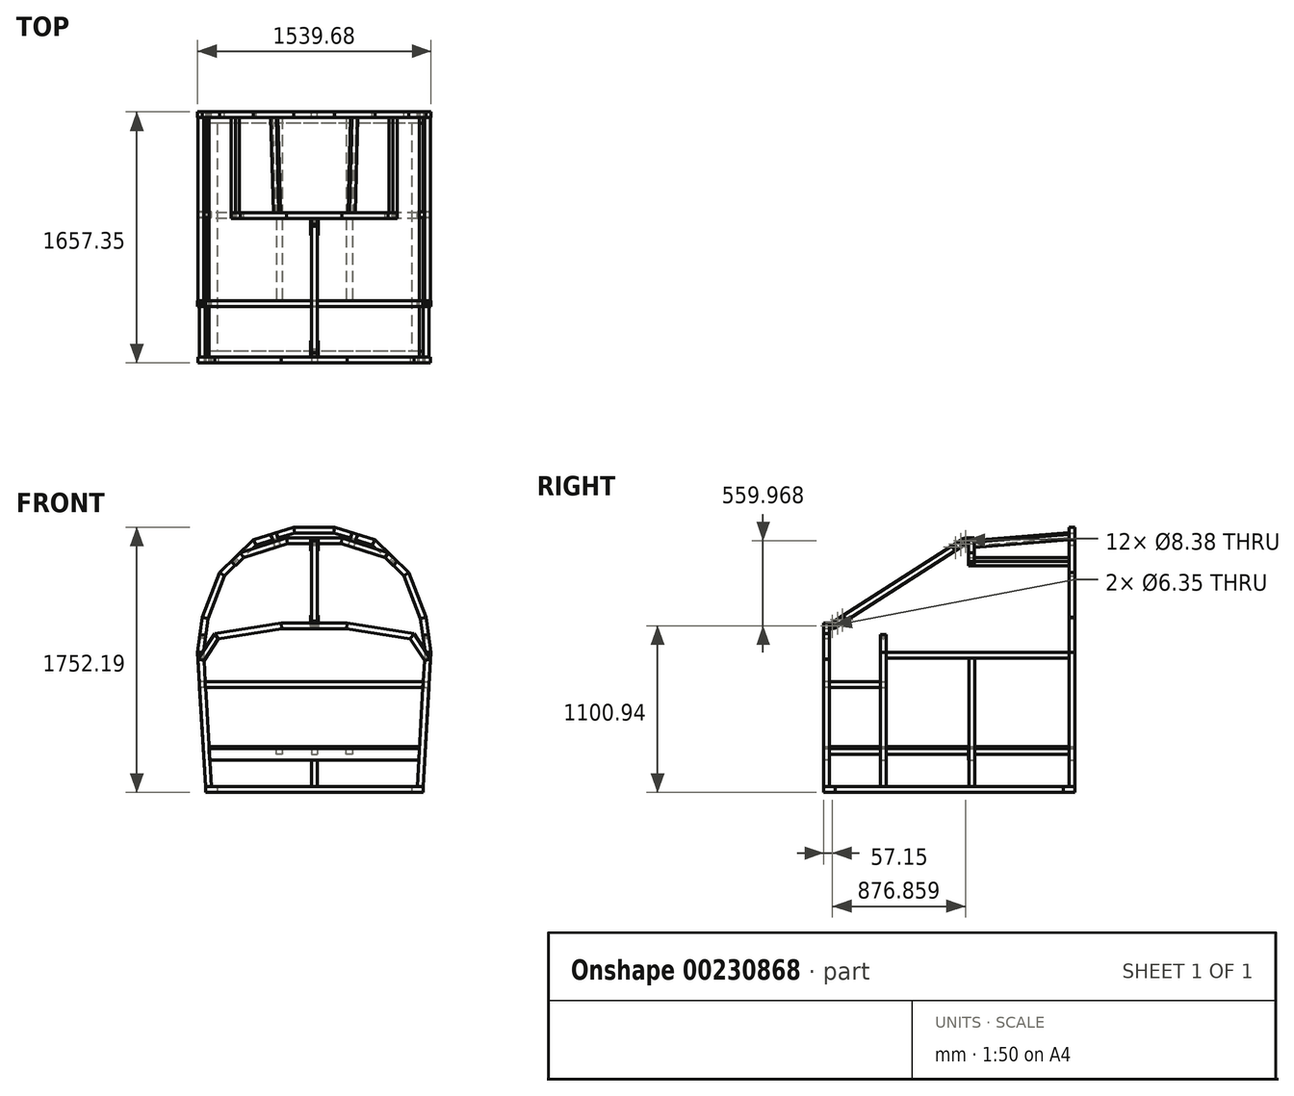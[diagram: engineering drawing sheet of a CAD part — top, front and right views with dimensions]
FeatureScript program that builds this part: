
annotation { "Feature Type Name" : "Feature", "Feature Type Description" : "" }
export const myFeature = defineFeature(function(context is Context, id is Id, definition is map)
    precondition{}
    {
        {
            var Q0;
            Q0=qCreatedBy(makeId("Front.planeOp"),FACE);
            var sketch = newSketch(context, id + "F0", { "sketchPlane" : qUnion([Q0])});
            skLineSegment(sketch, "E0", {"start": v(0, 0) * mm, "end": v(717.55, 0) * mm});
            skLineSegment(sketch, "E1", {"start": v(717.55, 0) * mm, "end": v(717.55, 38.1) * mm});
            skLineSegment(sketch, "E2", {"start": v(717.55, 38.1) * mm, "end": v(0, 38.1) * mm});
            skLineSegment(sketch, "E3.MirrorCS", {"start": v(-717.55, 38.1) * mm, "end": v(0, 38.1) * mm});
            skLineSegment(sketch, "E4.MirrorCS", {"start": v(0, 0) * mm, "end": v(-717.55, 0) * mm});
            skLineSegment(sketch, "E5.MirrorCS", {"start": v(-717.55, 0) * mm, "end": v(-717.55, 38.1) * mm});
            skSolve(sketch);
        }
        {
            var Q0;
            Q0 = qSketchRegion(id + "F0", true);
            extrude(context, id + "F1", {"entities" : qUnion([Q0]), "oppositeDirection" : true, "depth" : 76.2 * mm});
        }
        {
            var Q0;
            Q0=makeQuery(id+"F1.opExtrude","CAP_FACE",FACE,{"disambiguationData":[OSD([sQuery(id+"F0.wireOp",EDGE,"E0"),sQuery(id+"F0.wireOp",EDGE,"E1"),sQuery(id+"F0.wireOp",EDGE,"E2"),sQuery(id+"F0.wireOp",EDGE,"E3.MirrorCS"),sQuery(id+"F0.wireOp",EDGE,"E4.MirrorCS"),sQuery(id+"F0.wireOp",EDGE,"E5.MirrorCS")])],"isStart":false});
            var sketch = newSketch(context, id + "F2", { "sketchPlane" : qUnion([Q0])});
            skLineSegment(sketch, "E6.bottom", {"start": v(-717.55, 38.1) * mm, "end": v(-641.35, 38.1) * mm});
            skLineSegment(sketch, "E6.top", {"start": v(-717.55, 0) * mm, "end": v(-641.35, 0) * mm});
            skLineSegment(sketch, "E6.left", {"start": v(-717.55, 38.1) * mm, "end": v(-717.55, 0) * mm});
            skLineSegment(sketch, "E6.right", {"start": v(-641.35, 38.1) * mm, "end": v(-641.35, 0) * mm});
            skLineSegment(sketch, "E7.MirrorCS", {"start": v(641.35, 38.1) * mm, "end": v(641.35, 0) * mm});
            skLineSegment(sketch, "E8.MirrorCS", {"start": v(717.55, 38.1) * mm, "end": v(717.55, 0) * mm});
            skLineSegment(sketch, "E9.MirrorCS", {"start": v(717.55, 0) * mm, "end": v(641.35, 0) * mm});
            skLineSegment(sketch, "E10.MirrorCS", {"start": v(717.55, 38.1) * mm, "end": v(641.35, 38.1) * mm});
            skSolve(sketch);
        }
        {
            var Q0;
            Q0 = qSketchRegion(id + "F2", true);
            extrude(context, id + "F3", {"entities" : qUnion([Q0]), "depth" : 1504.95 * mm});
        }
        {
            var Q0;
            Q0=makeQuery(id+"F3.opExtrude","CAP_FACE",FACE,{"disambiguationData":[OSD([sQuery(id+"F2.wireOp",EDGE,"E6.bottom"),sQuery(id+"F2.wireOp",EDGE,"E6.top"),sQuery(id+"F2.wireOp",EDGE,"E6.left"),sQuery(id+"F2.wireOp",EDGE,"E6.right")])],"isStart":false});
            var sketch = newSketch(context, id + "F4", { "sketchPlane" : qUnion([Q0])});
            skPoint(sketch, "E11.0", {"position": v(717.55, 0) * mm});
            skLineSegment(sketch, "E12.bottom", {"start": v(-717.55, 38.1) * mm, "end": v(717.55, 38.1) * mm});
            skLineSegment(sketch, "E12.top", {"start": v(-717.55, 0) * mm, "end": v(717.55, 0) * mm});
            skLineSegment(sketch, "E12.left", {"start": v(-717.55, 38.1) * mm, "end": v(-717.55, 0) * mm});
            skLineSegment(sketch, "E12.right", {"start": v(717.55, 38.1) * mm, "end": v(717.55, 0) * mm});
            skSolve(sketch);
        }
        {
            var Q0;
            Q0 = qSketchRegion(id + "F4", true);
            extrude(context, id + "F5", {"entities" : qUnion([Q0]), "depth" : 76.2 * mm});
        }
        {
            var Q0;
            Q0=makeQuery(id+"F5.opExtrude","CAP_FACE",FACE,{"disambiguationData":[OSD([sQuery(id+"F4.wireOp",EDGE,"E12.bottom"),sQuery(id+"F4.wireOp",EDGE,"E12.top"),sQuery(id+"F4.wireOp",EDGE,"E12.left"),sQuery(id+"F4.wireOp",EDGE,"E12.right")])],"isStart":false});
            var sketch = newSketch(context, id + "F6", { "sketchPlane" : qUnion([Q0])});
            skLineSegment(sketch, "E13", {"start": v(-717.55, 290.98) * mm, "end": v(717.55, 290.98) * mm, "construction": true});
            skPoint(sketch, "E13.startSnap0", {"position": v(-717.55, 19.05) * mm});
            skPoint(sketch, "E14", {"position": v(-769.84, 926.08) * mm});
            skLineSegment(sketch, "E15", {"start": v(-769.84, 926.08) * mm, "end": v(-717.55, 38.1) * mm});
            skLineSegment(sketch, "E16", {"start": v(-717.55, 38.1) * mm, "end": v(-772.22, 38.1) * mm, "construction": true});
            skLineSegment(sketch, "E17.0", {"start": v(-731.59, 924.59) * mm, "end": v(-679.38, 38.1) * mm});
            skLineSegment(sketch, "E18", {"start": v(-717.55, 38.1) * mm, "end": v(-679.38, 38.1) * mm});
            skPoint(sketch, "E19", {"position": v(-737.87, 1158.11) * mm});
            skLineSegment(sketch, "E20", {"start": v(-769.84, 926.08) * mm, "end": v(-737.87, 1158.11) * mm});
            skLineSegment(sketch, "E21", {"start": v(-769.84, 926.08) * mm, "end": v(-776.64, 1041.51) * mm, "construction": true});
            skPoint(sketch, "E22", {"position": v(-623.49, 1451.13) * mm});
            skLineSegment(sketch, "E23", {"start": v(-737.87, 1158.11) * mm, "end": v(-623.49, 1451.13) * mm});
            skLineSegment(sketch, "E24", {"start": v(-737.87, 1158.11) * mm, "end": v(-724.69, 1253.8) * mm, "construction": true});
            skPoint(sketch, "E25", {"position": v(-133.82, 1752.2) * mm});
            skPoint(sketch, "E26", {"position": v(-402.75, 1667.92) * mm});
            skLineSegment(sketch, "E27", {"start": v(-623.49, 1451.13) * mm, "end": v(-402.75, 1667.92) * mm});
            skLineSegment(sketch, "E28", {"start": v(-623.49, 1451.13) * mm, "end": v(-586.53, 1545.8) * mm, "construction": true});
            skLineSegment(sketch, "E29", {"start": v(-402.75, 1667.92) * mm, "end": v(-133.82, 1752.2) * mm});
            skLineSegment(sketch, "E30", {"start": v(-402.75, 1667.92) * mm, "end": v(-358.73, 1711.15) * mm, "construction": true});
            skLineSegment(sketch, "E31", {"start": v(-133.82, 1752.2) * mm, "end": v(0, 1752.2) * mm});
            skLineSegment(sketch, "E32", {"start": v(-133.82, 1752.2) * mm, "end": v(-83.59, 1767.94) * mm, "construction": true});
            skLineSegment(sketch, "E33.0", {"start": v(-128, 1714.1) * mm, "end": v(0, 1714.1) * mm});
            skLineSegment(sketch, "E33.1", {"start": v(-731.59, 924.59) * mm, "end": v(-700.74, 1148.45) * mm});
            skLineSegment(sketch, "E33.2", {"start": v(-700.74, 1148.45) * mm, "end": v(-590.96, 1429.67) * mm});
            skLineSegment(sketch, "E33.3", {"start": v(-590.96, 1429.67) * mm, "end": v(-382.6, 1634.3) * mm});
            skLineSegment(sketch, "E33.4", {"start": v(-382.6, 1634.3) * mm, "end": v(-128, 1714.1) * mm});
            skLineSegment(sketch, "E34", {"start": v(-737.87, 1158.11) * mm, "end": v(-700.74, 1148.45) * mm});
            skLineSegment(sketch, "E35", {"start": v(-623.49, 1451.13) * mm, "end": v(-590.96, 1429.67) * mm});
            skLineSegment(sketch, "E36", {"start": v(-402.75, 1667.92) * mm, "end": v(-382.6, 1634.3) * mm});
            skLineSegment(sketch, "E37", {"start": v(-133.82, 1752.2) * mm, "end": v(-128, 1714.1) * mm});
            skLineSegment(sketch, "E38.MirrorCS", {"start": v(133.82, 1752.2) * mm, "end": v(0, 1752.2) * mm});
            skLineSegment(sketch, "E39.MirrorCS", {"start": v(128, 1714.1) * mm, "end": v(0, 1714.1) * mm});
            skLineSegment(sketch, "E40.MirrorCS", {"start": v(133.82, 1752.2) * mm, "end": v(128, 1714.1) * mm});
            skPoint(sketch, "E41.orphan", {"position": v(-731.67, 926.08) * mm});
            skLineSegment(sketch, "E42", {"start": v(-769.84, 926.08) * mm, "end": v(-731.59, 924.59) * mm});
            skLineSegment(sketch, "E43", {"start": v(0, 290.98) * mm, "end": v(-694.28, 290.98) * mm});
            skLineSegment(sketch, "E44", {"start": v(-689.79, 214.78) * mm, "end": v(0, 214.78) * mm});
            skLineSegment(sketch, "E45", {"start": v(-694.28, 290.98) * mm, "end": v(-689.79, 214.78) * mm});
            skLineSegment(sketch, "E46.MirrorCS", {"start": v(689.79, 214.78) * mm, "end": v(0, 214.78) * mm});
            skLineSegment(sketch, "E47.MirrorCS", {"start": v(0, 290.98) * mm, "end": v(694.28, 290.98) * mm});
            skLineSegment(sketch, "E48.MirrorCS", {"start": v(694.28, 290.98) * mm, "end": v(689.79, 214.78) * mm});
            skSolve(sketch);
        }
        {
            var Q0;
            Q0=makeQuery(id+"F6.imprint","IMPRINT",FACE,{"disambiguationData":[TD([[makeQuery(id+"F6.imprint","IMPRINT",EDGE,{"derivedFrom":sQuery(id+"F6.wireOp",EDGE,"E15")}),1.0]])]});
            extrude(context, id + "F7", {"entities" : qUnion([Q0]), "oppositeDirection" : true, "depth" : 38.1 * mm});
        }
        {
            var Q0;
            Q0=makeQuery(id+"F6.imprint","IMPRINT",FACE,{"disambiguationData":[TD([[makeQuery(id+"F6.imprint","IMPRINT",EDGE,{"derivedFrom":sQuery(id+"F6.wireOp",EDGE,"E20")}),-1.0]])]});
            extrude(context, id + "F8", {"entities" : qUnion([Q0]), "oppositeDirection" : true, "depth" : 38.1 * mm});
        }
        {
            var Q0;
            Q0=makeQuery(id+"F6.imprint","IMPRINT",FACE,{"disambiguationData":[TD([[makeQuery(id+"F6.imprint","IMPRINT",EDGE,{"derivedFrom":sQuery(id+"F6.wireOp",EDGE,"E23")}),-1.0]])]});
            extrude(context, id + "F9", {"entities" : qUnion([Q0]), "oppositeDirection" : true, "depth" : 38.1 * mm});
        }
        {
            var Q0;
            Q0=makeQuery(id+"F6.imprint","IMPRINT",FACE,{"disambiguationData":[TD([[makeQuery(id+"F6.imprint","IMPRINT",EDGE,{"derivedFrom":sQuery(id+"F6.wireOp",EDGE,"E27")}),-1.0]])]});
            extrude(context, id + "F10", {"entities" : qUnion([Q0]), "oppositeDirection" : true, "depth" : 38.1 * mm});
        }
        {
            var Q0;
            Q0=makeQuery(id+"F6.imprint","IMPRINT",FACE,{"disambiguationData":[TD([[makeQuery(id+"F6.imprint","IMPRINT",EDGE,{"derivedFrom":sQuery(id+"F6.wireOp",EDGE,"E29")}),-1.0]])]});
            extrude(context, id + "F11", {"entities" : qUnion([Q0]), "oppositeDirection" : true, "depth" : 38.1 * mm});
        }
        {
            var Q0;
            Q0=makeQuery(id+"F6.imprint","IMPRINT",FACE,{"disambiguationData":[TD([[makeQuery(id+"F6.imprint","IMPRINT",EDGE,{"derivedFrom":sQuery(id+"F6.wireOp",EDGE,"E31")}),-1.0]])]});
            extrude(context, id + "F12", {"entities" : qUnion([Q0]), "oppositeDirection" : true, "depth" : 38.1 * mm});
        }
        {
            var Q0;
            Q0=makeQuery(id+"F11.opExtrude","SWEPT_BODY",BODY,{"disambiguationData":[OSD([sQuery(id+"F6.wireOp",EDGE,"E29"),sQuery(id+"F6.wireOp",EDGE,"E33.4"),sQuery(id+"F6.wireOp",EDGE,"E36"),sQuery(id+"F6.wireOp",EDGE,"E37")])]});
            var Q1;
            Q1=makeQuery(id+"F10.opExtrude","SWEPT_BODY",BODY,{"disambiguationData":[OSD([sQuery(id+"F6.wireOp",EDGE,"E27"),sQuery(id+"F6.wireOp",EDGE,"E33.3"),sQuery(id+"F6.wireOp",EDGE,"E35"),sQuery(id+"F6.wireOp",EDGE,"E36")])]});
            var Q2;
            Q2=makeQuery(id+"F9.opExtrude","SWEPT_BODY",BODY,{"disambiguationData":[OSD([sQuery(id+"F6.wireOp",EDGE,"E23"),sQuery(id+"F6.wireOp",EDGE,"E33.2"),sQuery(id+"F6.wireOp",EDGE,"E34"),sQuery(id+"F6.wireOp",EDGE,"E35")])]});
            var Q3;
            Q3=makeQuery(id+"F8.opExtrude","SWEPT_BODY",BODY,{"disambiguationData":[OSD([sQuery(id+"F6.wireOp",EDGE,"E17.0"),sQuery(id+"F6.wireOp",EDGE,"o8qpjORA-LuDr-6oHj-oAAQ-A8CSd3xH4wH6"),sQuery(id+"F6.wireOp",EDGE,"E20"),sQuery(id+"F6.wireOp",EDGE,"E33.1"),sQuery(id+"F6.wireOp",EDGE,"E34")])]});
            var Q4;
            Q4=makeQuery(id+"F7.opExtrude","SWEPT_BODY",BODY,{"disambiguationData":[OSD([sQuery(id+"F6.wireOp",EDGE,"E15"),sQuery(id+"F6.wireOp",EDGE,"E17.0"),sQuery(id+"F6.wireOp",EDGE,"o8qpjORA-LuDr-6oHj-oAAQ-A8CSd3xH4wH6"),sQuery(id+"F6.wireOp",EDGE,"E18")])]});
            var Q5;
            Q5=qCreatedBy(makeId("Right.planeOp"),FACE);
            mirror(context, id + "F13", {"entities" : qUnion([Q0, Q1, Q2, Q3, Q4]), "mirrorPlane" : qUnion([Q5])});
        }
        {
            var Q0;
            {var subQ0=sQuery(id+"F6.wireOp",EDGE,"E18");Q0=makeQuery(id+"F6.imprint","IMPRINT",FACE,{"disambiguationData":[TD([[makeQuery(id+"F6.imprint","IMPRINT",EDGE,{"derivedFrom":subQ0}),-1.0]])]});}
            cPlane(context, id + "F14", {"entities" : qUnion([Q0]), "cplaneType" : CPlaneType.OFFSET, "offset" : 666.2 * mm, "oppositeDirection" : true, "width" : 152.4 * mm, "height" : 152.4 * mm});
        }
        {
            var Q0;
            Q0=qCreatedBy(id+"F14.planeOp",FACE);
            cPlane(context, id + "F15", {"entities" : qUnion([Q0]), "cplaneType" : CPlaneType.OFFSET, "offset" : 14.1 * mm, "oppositeDirection" : true, "width" : 152.4 * mm, "height" : 152.4 * mm});
        }
        {
            var Q0;
            Q0=qCreatedBy(id+"F14.planeOp",FACE);
            var sketch = newSketch(context, id + "F16", { "sketchPlane" : qUnion([Q0])});
            skLineSegment(sketch, "E49.0.1", {"start": v(-769.84, 926.08) * mm, "end": v(-769.69, 923.47) * mm});
            skLineSegment(sketch, "E49.0.2", {"start": v(-717.55, 38.1) * mm, "end": v(-679.38, 38.1) * mm});
            skLineSegment(sketch, "E49.0.3", {"start": v(-679.38, 38.1) * mm, "end": v(-729.34, 886.49) * mm});
            skLineSegment(sketch, "E50.bottom", {"start": v(-731.59, 924.59) * mm, "end": v(-769.69, 924.59) * mm, "construction": true});
            skLineSegment(sketch, "E50.top", {"start": v(-731.59, 886.49) * mm, "end": v(-769.69, 886.49) * mm, "construction": true});
            skLineSegment(sketch, "E50.left", {"start": v(-731.59, 924.59) * mm, "end": v(-731.59, 886.49) * mm, "construction": true});
            skLineSegment(sketch, "E50.right", {"start": v(-769.69, 924.59) * mm, "end": v(-769.69, 886.49) * mm, "construction": true});
            skLineSegment(sketch, "E51", {"start": v(-729.34, 886.49) * mm, "end": v(-767.5, 886.49) * mm});
            skLineSegment(sketch, "E52.trimOffspring", {"start": v(-767.5, 886.49) * mm, "end": v(-717.55, 38.1) * mm});
            skPoint(sketch, "E53", {"position": v(0, 1679.96) * mm});
            skLineSegment(sketch, "E54", {"start": v(-183.64, 1679.96) * mm, "end": v(183.64, 1679.96) * mm});
            skPoint(sketch, "E55", {"position": v(-486.73, 1583.66) * mm});
            skLineSegment(sketch, "E56", {"start": v(-183.64, 1679.96) * mm, "end": v(-486.73, 1583.66) * mm});
            skPoint(sketch, "E57", {"position": v(-546.95, 1525.4) * mm});
            skLineSegment(sketch, "E58", {"start": v(-486.73, 1583.66) * mm, "end": v(-546.95, 1525.4) * mm});
            skLineSegment(sketch, "E59", {"start": v(-466.67, 1550.06) * mm, "end": v(-177.74, 1641.86) * mm});
            skLineSegment(sketch, "E60.0", {"start": v(-177.74, 1641.86) * mm, "end": v(177.74, 1641.86) * mm});
            skLineSegment(sketch, "E61", {"start": v(-183.64, 1679.96) * mm, "end": v(-177.74, 1641.86) * mm});
            skLineSegment(sketch, "E62.MirrorCS", {"start": v(183.64, 1679.96) * mm, "end": v(177.74, 1641.86) * mm});
            skLineSegment(sketch, "E63.0", {"start": v(-466.67, 1550.06) * mm, "end": v(-520.46, 1498.02) * mm});
            skLineSegment(sketch, "E64", {"start": v(-546.95, 1525.4) * mm, "end": v(-520.46, 1498.02) * mm});
            skLineSegment(sketch, "E65", {"start": v(-486.73, 1583.66) * mm, "end": v(-466.67, 1550.06) * mm});
            skSolve(sketch);
        }
        {
            var Q0;
            Q0=qCreatedBy(id+"F15.planeOp",FACE);
            var sketch = newSketch(context, id + "F17", { "sketchPlane" : qUnion([Q0])});
            skLineSegment(sketch, "E66.0.0", {"start": v(-729.34, 886.49) * mm, "end": v(-767.5, 886.49) * mm});
            skLineSegment(sketch, "E66.0.1", {"start": v(-767.5, 886.49) * mm, "end": v(-717.55, 38.1) * mm});
            skLineSegment(sketch, "E66.0.2", {"start": v(-717.55, 38.1) * mm, "end": v(-679.38, 38.1) * mm});
            skLineSegment(sketch, "E66.0.3", {"start": v(-679.38, 38.1) * mm, "end": v(-729.34, 886.49) * mm});
            skSolve(sketch);
        }
        {
            var Q0;
            Q0=makeQuery(id+"F17.imprint","IMPRINT",FACE,{"disambiguationData":[TD([[makeQuery(id+"F17.imprint","IMPRINT",EDGE,{"derivedFrom":sQuery(id+"F17.wireOp",EDGE,"E66.0.0")}),1.0]])]});
            extrude(context, id + "F18", {"entities" : qUnion([Q0]), "oppositeDirection" : true, "depth" : 38.1 * mm, "symmetric" : true});
        }
        {
            var Q0;
            Q0=makeQuery(id+"F18.opExtrude","SWEPT_BODY",BODY,{"disambiguationData":[OSD([sQuery(id+"F17.wireOp",EDGE,"E66.0.0"),sQuery(id+"F17.wireOp",EDGE,"E66.0.1"),sQuery(id+"F17.wireOp",EDGE,"E66.0.2"),sQuery(id+"F17.wireOp",EDGE,"E66.0.3")])]});
            var Q1;
            Q1=qCreatedBy(makeId("Right.planeOp"),FACE);
            mirror(context, id + "F19", {"entities" : qUnion([Q0]), "mirrorPlane" : qUnion([Q1])});
        }
        {
            var Q0;
            Q0=makeQuery(id+"F16.imprint","IMPRINT",FACE,{"disambiguationData":[TD([[makeQuery(id+"F16.imprint","IMPRINT",EDGE,{"derivedFrom":sQuery(id+"F16.wireOp",EDGE,"E56")}),1.0]])]});
            extrude(context, id + "F20", {"entities" : qUnion([Q0]), "oppositeDirection" : true, "depth" : 38.1 * mm});
        }
        {
            var Q0;
            Q0=makeQuery(id+"F16.imprint","IMPRINT",FACE,{"disambiguationData":[TD([[makeQuery(id+"F16.imprint","IMPRINT",EDGE,{"derivedFrom":sQuery(id+"F16.wireOp",EDGE,"E54")}),-1.0]])]});
            extrude(context, id + "F21", {"entities" : qUnion([Q0]), "oppositeDirection" : true, "depth" : 38.1 * mm});
        }
        {
            var Q0;
            Q0=makeQuery(id+"F20.opExtrude","SWEPT_BODY",BODY,{"disambiguationData":[OSD([sQuery(id+"F16.wireOp",EDGE,"E56"),sQuery(id+"F16.wireOp",EDGE,"57TPLywA-1E1Z-HFSi-5JsW-R5pV3Np6fluj"),sQuery(id+"F16.wireOp",EDGE,"E59"),sQuery(id+"F16.wireOp",EDGE,"E61")])]});
            var Q1;
            Q1=qCreatedBy(makeId("Right.planeOp"),FACE);
            mirror(context, id + "F22", {"entities" : qUnion([Q0]), "mirrorPlane" : qUnion([Q1])});
        }
        {
            var Q0;
            Q0=qCreatedBy(id+"F14.planeOp",FACE);
            cPlane(context, id + "F23", {"entities" : qUnion([Q0]), "cplaneType" : CPlaneType.OFFSET, "offset" : 580.1 * mm, "oppositeDirection" : true, "width" : 152.4 * mm, "height" : 152.4 * mm});
        }
        {
            var Q0;
            Q0=qCreatedBy(id+"F23.planeOp",FACE);
            var sketch = newSketch(context, id + "F24", { "sketchPlane" : qUnion([Q0])});
            skLineSegment(sketch, "E67.0.0", {"start": v(-731.59, 924.59) * mm, "end": v(-769.84, 926.08) * mm});
            skLineSegment(sketch, "E67.0.1", {"start": v(-769.84, 926.08) * mm, "end": v(-717.55, 38.1) * mm});
            skLineSegment(sketch, "E67.0.2", {"start": v(-717.55, 38.1) * mm, "end": v(-679.38, 38.1) * mm});
            skLineSegment(sketch, "E67.0.3", {"start": v(-679.38, 38.1) * mm, "end": v(-731.59, 924.59) * mm});
            skPoint(sketch, "E68", {"position": v(-754.13, 1043.69) * mm});
            skLineSegment(sketch, "E69", {"start": v(-754.13, 1043.69) * mm, "end": v(-769.84, 926.08) * mm});
            skLineSegment(sketch, "E70", {"start": v(-754.13, 1043.69) * mm, "end": v(-716.37, 1038.64) * mm});
            skLineSegment(sketch, "E71", {"start": v(-716.37, 1038.64) * mm, "end": v(-731.59, 924.59) * mm});
            skLineSegment(sketch, "E72", {"start": v(-720.17, 730.7) * mm, "end": v(0, 730.7) * mm});
            skLineSegment(sketch, "E73", {"start": v(-717.92, 692.6) * mm, "end": v(0, 692.6) * mm});
            skLineSegment(sketch, "E74", {"start": v(-720.17, 730.7) * mm, "end": v(-717.92, 692.6) * mm});
            skLineSegment(sketch, "E75.MirrorCS", {"start": v(717.92, 692.6) * mm, "end": v(0, 692.6) * mm});
            skLineSegment(sketch, "E76.MirrorCS", {"start": v(720.17, 730.7) * mm, "end": v(0, 730.7) * mm});
            skLineSegment(sketch, "E77.MirrorCS", {"start": v(720.17, 730.7) * mm, "end": v(717.92, 692.6) * mm});
            skSolve(sketch);
        }
        {
            var Q0;
            Q0=makeQuery(id+"F24.imprint","IMPRINT",FACE,{"disambiguationData":[TD([[makeQuery(id+"F24.imprint","IMPRINT",EDGE,{"derivedFrom":sQuery(id+"F24.wireOp",EDGE,"E67.0.0")}),1.0]])]});
            extrude(context, id + "F25", {"entities" : qUnion([Q0]), "oppositeDirection" : true, "depth" : 38.1 * mm});
        }
        {
            var Q0;
            Q0=makeQuery(id+"F24.imprint","IMPRINT",FACE,{"disambiguationData":[TD([[makeQuery(id+"F24.imprint","IMPRINT",EDGE,{"derivedFrom":sQuery(id+"F24.wireOp",EDGE,"E67.0.0")}),-1.0]])]});
            extrude(context, id + "F26", {"entities" : qUnion([Q0]), "oppositeDirection" : true, "depth" : 38.1 * mm});
        }
        {
            var Q0;
            Q0=makeQuery(id+"F25.opExtrude","SWEPT_BODY",BODY,{"disambiguationData":[OSD([sQuery(id+"F24.wireOp",EDGE,"E67.0.0"),sQuery(id+"F24.wireOp",EDGE,"E67.0.1"),sQuery(id+"F24.wireOp",EDGE,"E67.0.2"),sQuery(id+"F24.wireOp",EDGE,"E67.0.3")])]});
            var Q1;
            Q1=makeQuery(id+"F26.opExtrude","SWEPT_BODY",BODY,{"disambiguationData":[OSD([sQuery(id+"F24.wireOp",EDGE,"E67.0.0"),sQuery(id+"F24.wireOp",EDGE,"E69"),sQuery(id+"F24.wireOp",EDGE,"E70"),sQuery(id+"F24.wireOp",EDGE,"E71")])]});
            var Q2;
            Q2=qCreatedBy(makeId("Right.planeOp"),FACE);
            mirror(context, id + "F27", {"entities" : qUnion([Q0, Q1]), "mirrorPlane" : qUnion([Q2])});
        }
        {
            var Q0;
            Q0=makeQuery(id+"F1.opExtrude","CAP_FACE",FACE,{"disambiguationData":[OSD([sQuery(id+"F0.wireOp",EDGE,"E0"),sQuery(id+"F0.wireOp",EDGE,"E1"),sQuery(id+"F0.wireOp",EDGE,"E2"),sQuery(id+"F0.wireOp",EDGE,"E3.MirrorCS"),sQuery(id+"F0.wireOp",EDGE,"E4.MirrorCS"),sQuery(id+"F0.wireOp",EDGE,"E5.MirrorCS")])],"isStart":true});
            var sketch = newSketch(context, id + "F28", { "sketchPlane" : qUnion([Q0])});
            skPoint(sketch, "E78", {"position": v(765.74, 881.1) * mm});
            skLineSegment(sketch, "E79", {"start": v(717.55, 38.1) * mm, "end": v(765.74, 881.1) * mm});
            skPoint(sketch, "E80", {"position": v(657.35, 1047.75) * mm});
            skLineSegment(sketch, "E81", {"start": v(657.35, 1047.75) * mm, "end": v(765.74, 881.1) * mm});
            skPoint(sketch, "E82", {"position": v(217.86, 1119.99) * mm});
            skLineSegment(sketch, "E83", {"start": v(217.86, 1119.99) * mm, "end": v(657.35, 1047.75) * mm});
            skLineSegment(sketch, "E84", {"start": v(217.86, 1119.99) * mm, "end": v(0, 1119.99) * mm});
            skLineSegment(sketch, "E85.0", {"start": v(214.75, 1081.89) * mm, "end": v(0, 1081.89) * mm});
            skLineSegment(sketch, "E85.1", {"start": v(214.75, 1081.89) * mm, "end": v(634.58, 1012.88) * mm});
            skLineSegment(sketch, "E85.2", {"start": v(634.58, 1012.88) * mm, "end": v(727, 870.8) * mm});
            skLineSegment(sketch, "E85.3", {"start": v(679.51, 40.27) * mm, "end": v(727, 870.8) * mm});
            skLineSegment(sketch, "E86", {"start": v(217.86, 1119.99) * mm, "end": v(214.75, 1081.89) * mm});
            skLineSegment(sketch, "E87", {"start": v(657.35, 1047.75) * mm, "end": v(634.58, 1012.88) * mm});
            skLineSegment(sketch, "E88", {"start": v(765.74, 881.1) * mm, "end": v(727, 870.8) * mm});
            skLineSegment(sketch, "E89", {"start": v(679.51, 40.27) * mm, "end": v(717.55, 38.1) * mm});
            skLineSegment(sketch, "E90.MirrorCS", {"start": v(-217.86, 1119.99) * mm, "end": v(0, 1119.99) * mm});
            skLineSegment(sketch, "E91.MirrorCS", {"start": v(-214.75, 1081.89) * mm, "end": v(0, 1081.89) * mm});
            skLineSegment(sketch, "E92.MirrorCS", {"start": v(-217.86, 1119.99) * mm, "end": v(-214.75, 1081.89) * mm});
            skLineSegment(sketch, "E93.0.0", {"start": v(0, 730.7) * mm, "end": v(720.17, 730.7) * mm});
            skLineSegment(sketch, "E93.0.1", {"start": v(720.17, 730.7) * mm, "end": v(717.92, 692.6) * mm});
            skLineSegment(sketch, "E93.0.2", {"start": v(717.92, 692.6) * mm, "end": v(0, 692.6) * mm});
            skLineSegment(sketch, "E93.0.3", {"start": v(0, 692.6) * mm, "end": v(-717.92, 692.6) * mm});
            skLineSegment(sketch, "E93.0.4", {"start": v(-717.92, 692.6) * mm, "end": v(-720.17, 730.7) * mm});
            skLineSegment(sketch, "E93.0.5", {"start": v(-720.17, 730.7) * mm, "end": v(0, 730.7) * mm});
            skSolve(sketch);
        }
        {
            var Q0;
            Q0=makeQuery(id+"F24.imprint","IMPRINT",FACE,{"disambiguationData":[TD([[makeQuery(id+"F24.imprint","IMPRINT",EDGE,{"derivedFrom":sQuery(id+"F24.wireOp",EDGE,"E72")}),-1.0]])]});
            extrude(context, id + "F29", {"entities" : qUnion([Q0]), "oppositeDirection" : true, "depth" : 38.1 * mm});
        }
        {
            var Q0;
            Q0=makeQuery(id+"F28.imprint","IMPRINT",FACE,{"disambiguationData":[TD([[makeQuery(id+"F28.imprint","IMPRINT",EDGE,{"derivedFrom":sQuery(id+"F28.wireOp",EDGE,"E79")}),1.0]])]});
            extrude(context, id + "F30", {"entities" : qUnion([Q0]), "oppositeDirection" : true, "depth" : 38.1 * mm});
        }
        {
            var Q0;
            Q0=makeQuery(id+"F28.imprint","IMPRINT",FACE,{"disambiguationData":[TD([[makeQuery(id+"F28.imprint","IMPRINT",EDGE,{"derivedFrom":sQuery(id+"F28.wireOp",EDGE,"E81")}),-1.0]])]});
            extrude(context, id + "F31", {"entities" : qUnion([Q0]), "oppositeDirection" : true, "depth" : 38.1 * mm});
        }
        {
            var Q0;
            Q0=makeQuery(id+"F28.imprint","IMPRINT",FACE,{"disambiguationData":[TD([[makeQuery(id+"F28.imprint","IMPRINT",EDGE,{"derivedFrom":sQuery(id+"F28.wireOp",EDGE,"E83")}),-1.0]])]});
            extrude(context, id + "F32", {"entities" : qUnion([Q0]), "oppositeDirection" : true, "depth" : 38.1 * mm});
        }
        {
            var Q0;
            Q0=makeQuery(id+"F28.imprint","IMPRINT",FACE,{"disambiguationData":[TD([[makeQuery(id+"F28.imprint","IMPRINT",EDGE,{"derivedFrom":sQuery(id+"F28.wireOp",EDGE,"E84")}),1.0]])]});
            extrude(context, id + "F33", {"entities" : qUnion([Q0]), "oppositeDirection" : true, "depth" : 38.1 * mm});
        }
        {
            var Q0;
            Q0=makeQuery(id+"F32.opExtrude","SWEPT_BODY",BODY,{"disambiguationData":[OSD([sQuery(id+"F28.wireOp",EDGE,"E83"),sQuery(id+"F28.wireOp",EDGE,"E85.1"),sQuery(id+"F28.wireOp",EDGE,"E86"),sQuery(id+"F28.wireOp",EDGE,"E87")])]});
            var Q1;
            Q1=makeQuery(id+"F31.opExtrude","SWEPT_BODY",BODY,{"disambiguationData":[OSD([sQuery(id+"F28.wireOp",EDGE,"E81"),sQuery(id+"F28.wireOp",EDGE,"E85.2"),sQuery(id+"F28.wireOp",EDGE,"E87"),sQuery(id+"F28.wireOp",EDGE,"E88")])]});
            var Q2;
            Q2=makeQuery(id+"F30.opExtrude","SWEPT_BODY",BODY,{"disambiguationData":[OSD([sQuery(id+"F28.wireOp",EDGE,"E79"),sQuery(id+"F28.wireOp",EDGE,"E85.3"),sQuery(id+"F28.wireOp",EDGE,"E88"),sQuery(id+"F28.wireOp",EDGE,"E89")])]});
            var Q3;
            Q3=qCreatedBy(makeId("Right.planeOp"),FACE);
            mirror(context, id + "F34", {"entities" : qUnion([Q0, Q1, Q2]), "mirrorPlane" : qUnion([Q3])});
        }
        {
            var Q0;
            {var subQ0=sQuery(id+"F28.wireOp",EDGE,"E93.0.3");Q0=makeQuery(id+"F28.imprint","IMPRINT",FACE,{"disambiguationData":[TD([[makeQuery(id+"F28.imprint","IMPRINT",EDGE,{"derivedFrom":subQ0}),-1.0]])]});}
            extrude(context, id + "F35", {"entities" : qUnion([Q0]), "oppositeDirection" : true, "depth" : 38.1 * mm});
        }
        {
            var Q0;
            Q0=makeQuery(id+"F25.opExtrude","CAP_FACE",FACE,{"disambiguationData":[OSD([sQuery(id+"F24.wireOp",EDGE,"E67.0.0"),sQuery(id+"F24.wireOp",EDGE,"E67.0.1"),sQuery(id+"F24.wireOp",EDGE,"E67.0.2"),sQuery(id+"F24.wireOp",EDGE,"E67.0.3"),sQuery(id+"F24.wireOp",EDGE,"E74")])],"isStart":false});
            var sketch = newSketch(context, id + "F36", { "sketchPlane" : qUnion([Q0])});
            skLineSegment(sketch, "E94.0.0", {"start": v(718.98, 730.7) * mm, "end": v(0, 730.7) * mm, "construction": true});
            skLineSegment(sketch, "E94.0.1", {"start": v(0, 730.7) * mm, "end": v(-720.17, 730.7) * mm, "construction": true});
            skLineSegment(sketch, "E94.0.2", {"start": v(-720.17, 730.7) * mm, "end": v(-717.92, 692.6) * mm, "construction": true});
            skLineSegment(sketch, "E94.0.3", {"start": v(-717.92, 692.6) * mm, "end": v(0, 692.6) * mm, "construction": true});
            skLineSegment(sketch, "E94.0.4", {"start": v(0, 692.6) * mm, "end": v(716.8, 692.6) * mm, "construction": true});
            skLineSegment(sketch, "E94.0.5", {"start": v(716.8, 692.6) * mm, "end": v(718.98, 730.7) * mm, "construction": true});
            skLineSegment(sketch, "E95.bottom", {"start": v(718.98, 730.7) * mm, "end": v(757.08, 730.7) * mm});
            skLineSegment(sketch, "E95.top", {"start": v(718.98, 692.6) * mm, "end": v(757.08, 692.6) * mm});
            skLineSegment(sketch, "E95.left", {"start": v(718.98, 730.7) * mm, "end": v(718.98, 692.6) * mm});
            skLineSegment(sketch, "E95.right", {"start": v(757.08, 730.7) * mm, "end": v(757.08, 692.6) * mm});
            skSolve(sketch);
        }
        {
            var Q0;
            Q0 = qSketchRegion(id + "F36", true);
            var Q1;
            Q1=makeQuery(id+"F30.opExtrude","CAP_FACE",FACE,{"disambiguationData":[OSD([sQuery(id+"F28.wireOp",EDGE,"E79"),sQuery(id+"F28.wireOp",EDGE,"E85.3"),sQuery(id+"F28.wireOp",EDGE,"E88"),sQuery(id+"F28.wireOp",EDGE,"E89"),sQuery(id+"F28.wireOp",EDGE,"E93.0.0"),sQuery(id+"F28.wireOp",EDGE,"E93.0.1"),sQuery(id+"F28.wireOp",EDGE,"E93.0.2")])],"isStart":false});
            extrude(context, id + "F37", {"entities" : qUnion([Q0]), "endBound" : BoundingType.UP_TO_SURFACE, "endBoundEntityFace" : qUnion([Q1]), "depth" : 25.4 * mm});
        }
        {
            var Q0;
            Q0=makeQuery(id+"F37.opExtrude","SWEPT_BODY",BODY,{"disambiguationData":[OSD([sQuery(id+"F36.wireOp",EDGE,"E95.bottom"),sQuery(id+"F36.wireOp",EDGE,"E95.top"),sQuery(id+"F36.wireOp",EDGE,"E95.left"),sQuery(id+"F36.wireOp",EDGE,"E95.right")])]});
            var Q1;
            Q1=qCreatedBy(makeId("Right.planeOp"),FACE);
            mirror(context, id + "F38", {"entities" : qUnion([Q0]), "mirrorPlane" : qUnion([Q1])});
        }
        {
            var Q0;
            Q0=makeQuery(id+"F7.opExtrude","CAP_FACE",FACE,{"disambiguationData":[OSD([sQuery(id+"F6.wireOp",EDGE,"E15"),sQuery(id+"F6.wireOp",EDGE,"E17.0"),sQuery(id+"F6.wireOp",EDGE,"E18"),sQuery(id+"F6.wireOp",EDGE,"E42")])],"isStart":false});
            var sketch = newSketch(context, id + "F39", { "sketchPlane" : qUnion([Q0])});
            skLineSegment(sketch, "E96.0", {"start": v(729.34, 886.49) * mm, "end": v(767.5, 886.49) * mm, "construction": true});
            skLineSegment(sketch, "E97.bottom", {"start": v(729.34, 886.49) * mm, "end": v(767.44, 886.49) * mm});
            skLineSegment(sketch, "E97.top", {"start": v(729.34, 924.59) * mm, "end": v(767.44, 924.59) * mm});
            skLineSegment(sketch, "E97.left", {"start": v(729.34, 886.49) * mm, "end": v(729.34, 924.59) * mm});
            skLineSegment(sketch, "E97.right", {"start": v(767.44, 886.49) * mm, "end": v(767.44, 924.59) * mm});
            skSolve(sketch);
        }
        {
            var Q0;
            Q0 = qSketchRegion(id + "F39", true);
            var Q1;
            Q1=makeQuery(id+"F25.opExtrude","CAP_FACE",FACE,{"disambiguationData":[OSD([sQuery(id+"F24.wireOp",EDGE,"E67.0.0"),sQuery(id+"F24.wireOp",EDGE,"E67.0.1"),sQuery(id+"F24.wireOp",EDGE,"E67.0.2"),sQuery(id+"F24.wireOp",EDGE,"E67.0.3"),sQuery(id+"F24.wireOp",EDGE,"E74")])],"isStart":true});
            extrude(context, id + "F40", {"entities" : qUnion([Q0]), "endBound" : BoundingType.UP_TO_SURFACE, "endBoundEntityFace" : qUnion([Q1]), "depth" : 25.4 * mm});
        }
        {
            var Q0;
            Q0=makeQuery(id+"F40.opExtrude","SWEPT_BODY",BODY,{"disambiguationData":[OSD([sQuery(id+"F39.wireOp",EDGE,"E97.bottom"),sQuery(id+"F39.wireOp",EDGE,"E97.top"),sQuery(id+"F39.wireOp",EDGE,"E97.left"),sQuery(id+"F39.wireOp",EDGE,"E97.right")])]});
            var Q1;
            Q1=qCreatedBy(makeId("Right.planeOp"),FACE);
            mirror(context, id + "F41", {"entities" : qUnion([Q0]), "mirrorPlane" : qUnion([Q1])});
        }
        {
            var Q0;
            Q0=makeQuery(id+"F16.imprint","IMPRINT",FACE,{"disambiguationData":[TD([[makeQuery(id+"F16.imprint","IMPRINT",EDGE,{"derivedFrom":sQuery(id+"F16.wireOp",EDGE,"E58")}),1.0]])]});
            extrude(context, id + "F42", {"entities" : qUnion([Q0]), "oppositeDirection" : true, "depth" : 38.1 * mm});
        }
        {
            var Q0;
            Q0=makeQuery(id+"F42.opExtrude","SWEPT_BODY",BODY,{"disambiguationData":[OSD([sQuery(id+"F16.wireOp",EDGE,"E58"),sQuery(id+"F16.wireOp",EDGE,"E63.0"),sQuery(id+"F16.wireOp",EDGE,"E64"),sQuery(id+"F16.wireOp",EDGE,"E65")])]});
            var Q1;
            Q1=qCreatedBy(makeId("Right.planeOp"),FACE);
            mirror(context, id + "F43", {"entities" : qUnion([Q0]), "mirrorPlane" : qUnion([Q1])});
        }
        {
            var Q0;
            Q0=makeQuery(id+"F16.imprint","IMPRINT",FACE,{"disambiguationData":[TD([[makeQuery(id+"F16.imprint","IMPRINT",EDGE,{"derivedFrom":sQuery(id+"F16.wireOp",EDGE,"E58")}),1.0]])]});
            var sketch = newSketch(context, id + "F44", { "sketchPlane" : qUnion([Q0])});
            skPoint(sketch, "E98.0", {"position": v(-546.95, 1525.4) * mm});
            skLineSegment(sketch, "E99.0", {"start": v(-486.73, 1583.66) * mm, "end": v(-546.95, 1525.4) * mm, "construction": true});
            skLineSegment(sketch, "E100.bottom", {"start": v(-546.95, 1525.4) * mm, "end": v(-519.57, 1551.9) * mm});
            skLineSegment(sketch, "E100.top", {"start": v(-520.46, 1498.02) * mm, "end": v(-493.08, 1524.5) * mm});
            skLineSegment(sketch, "E100.left", {"start": v(-546.95, 1525.4) * mm, "end": v(-520.46, 1498.02) * mm});
            skLineSegment(sketch, "E100.right", {"start": v(-519.57, 1551.9) * mm, "end": v(-493.08, 1524.5) * mm});
            skSolve(sketch);
        }
        {
            var Q0;
            Q0 = qSketchRegion(id + "F44", true);
            var Q1;
            Q1=makeQuery(id+"F10.opExtrude","CAP_FACE",FACE,{"disambiguationData":[OSD([sQuery(id+"F6.wireOp",EDGE,"E27"),sQuery(id+"F6.wireOp",EDGE,"E33.3"),sQuery(id+"F6.wireOp",EDGE,"E35"),sQuery(id+"F6.wireOp",EDGE,"E36")])],"isStart":false});
            extrude(context, id + "F45", {"entities" : qUnion([Q0]), "endBound" : BoundingType.UP_TO_SURFACE, "endBoundEntityFace" : qUnion([Q1]), "depth" : 25.4 * mm});
        }
        {
            var Q0;
            Q0=makeQuery(id+"F45.opExtrude","SWEPT_BODY",BODY,{"disambiguationData":[OSD([sQuery(id+"F44.wireOp",EDGE,"E100.bottom"),sQuery(id+"F44.wireOp",EDGE,"E100.top"),sQuery(id+"F44.wireOp",EDGE,"E100.left"),sQuery(id+"F44.wireOp",EDGE,"E100.right")])]});
            var Q1;
            Q1=qCreatedBy(makeId("Right.planeOp"),FACE);
            mirror(context, id + "F46", {"entities" : qUnion([Q0]), "mirrorPlane" : qUnion([Q1])});
        }
        {
            var Q0;
            Q0=makeQuery(id+"F11.opExtrude","CAP_FACE",FACE,{"disambiguationData":[OSD([sQuery(id+"F6.wireOp",EDGE,"E29"),sQuery(id+"F6.wireOp",EDGE,"E33.4"),sQuery(id+"F6.wireOp",EDGE,"E36"),sQuery(id+"F6.wireOp",EDGE,"E37")])],"isStart":false});
            var sketch = newSketch(context, id + "F47", { "sketchPlane" : qUnion([Q0])});
            skLineSegment(sketch, "E101", {"start": v(268.29, 1710.06) * mm, "end": v(256.9, 1673.7) * mm, "construction": true});
            skPoint(sketch, "E102", {"position": v(262.59, 1691.88) * mm});
            skLineSegment(sketch, "E103.bottom", {"start": v(286.46, 1704.36) * mm, "end": v(250.1, 1715.75) * mm});
            skLineSegment(sketch, "E103.top", {"start": v(275.07, 1668) * mm, "end": v(238.71, 1679.4) * mm});
            skLineSegment(sketch, "E103.left", {"start": v(286.46, 1704.36) * mm, "end": v(275.07, 1668) * mm});
            skLineSegment(sketch, "E103.right", {"start": v(250.1, 1715.75) * mm, "end": v(238.71, 1679.4) * mm});
            skLineSegment(sketch, "E104.MirrorCS", {"start": v(-250.1, 1715.75) * mm, "end": v(-238.71, 1679.4) * mm});
            skLineSegment(sketch, "E105.MirrorCS", {"start": v(-286.46, 1704.36) * mm, "end": v(-250.1, 1715.75) * mm});
            skLineSegment(sketch, "E106.MirrorCS", {"start": v(-286.46, 1704.36) * mm, "end": v(-275.07, 1668) * mm});
            skLineSegment(sketch, "E107.MirrorCS", {"start": v(-275.07, 1668) * mm, "end": v(-238.71, 1679.4) * mm});
            skSolve(sketch);
        }
        {
            var Q0;
            Q0=makeQuery(id+"F16.imprint","IMPRINT",FACE,{"disambiguationData":[TD([[makeQuery(id+"F16.imprint","IMPRINT",EDGE,{"derivedFrom":sQuery(id+"F16.wireOp",EDGE,"E56")}),1.0]])]});
            var sketch = newSketch(context, id + "F48", { "sketchPlane" : qUnion([Q0])});
            skLineSegment(sketch, "E108.0", {"start": v(-286.46, 1704.36) * mm, "end": v(-275.07, 1668) * mm, "construction": true});
            skLineSegment(sketch, "E109.0", {"start": v(-250.1, 1715.75) * mm, "end": v(-238.71, 1679.4) * mm, "construction": true});
            skLineSegment(sketch, "E110.0", {"start": v(250.1, 1715.75) * mm, "end": v(238.71, 1679.4) * mm, "construction": true});
            skLineSegment(sketch, "E111.0", {"start": v(286.46, 1704.36) * mm, "end": v(275.07, 1668) * mm, "construction": true});
            skLineSegment(sketch, "E112.0.0", {"start": v(-486.73, 1583.66) * mm, "end": v(-466.67, 1550.06) * mm, "construction": true});
            skLineSegment(sketch, "E112.0.1", {"start": v(-466.67, 1550.06) * mm, "end": v(-177.74, 1641.86) * mm, "construction": true});
            skLineSegment(sketch, "E112.0.2", {"start": v(-177.74, 1641.86) * mm, "end": v(-183.64, 1679.96) * mm, "construction": true});
            skLineSegment(sketch, "E112.0.3", {"start": v(-183.64, 1679.96) * mm, "end": v(-486.73, 1583.66) * mm, "construction": true});
            skLineSegment(sketch, "E113.0.0", {"start": v(466.67, 1550.06) * mm, "end": v(486.73, 1583.66) * mm, "construction": true});
            skLineSegment(sketch, "E113.0.1", {"start": v(486.73, 1583.66) * mm, "end": v(183.64, 1679.96) * mm, "construction": true});
            skLineSegment(sketch, "E113.0.2", {"start": v(183.64, 1679.96) * mm, "end": v(177.74, 1641.86) * mm, "construction": true});
            skLineSegment(sketch, "E113.0.3", {"start": v(177.74, 1641.86) * mm, "end": v(466.67, 1550.06) * mm, "construction": true});
            skLineSegment(sketch, "E114", {"start": v(-270.14, 1652.48) * mm, "end": v(-258.6, 1616.16) * mm});
            skLineSegment(sketch, "E115", {"start": v(-233.83, 1664.01) * mm, "end": v(-222.3, 1627.7) * mm});
            skLineSegment(sketch, "E116", {"start": v(-270.14, 1652.48) * mm, "end": v(-233.83, 1664.01) * mm});
            skLineSegment(sketch, "E117", {"start": v(-258.6, 1616.16) * mm, "end": v(-222.3, 1627.7) * mm});
            skLineSegment(sketch, "E118.MirrorCS", {"start": v(270.14, 1652.48) * mm, "end": v(258.6, 1616.16) * mm});
            skLineSegment(sketch, "E119.MirrorCS", {"start": v(233.83, 1664.01) * mm, "end": v(222.3, 1627.7) * mm});
            skLineSegment(sketch, "E120", {"start": v(233.83, 1664.01) * mm, "end": v(270.14, 1652.48) * mm});
            skLineSegment(sketch, "E121", {"start": v(222.3, 1627.7) * mm, "end": v(258.6, 1616.16) * mm});
            skSolve(sketch);
        }
        {
            var Q0;
            Q0=makeQuery(id+"F47.imprint","IMPRINT",FACE,{"disambiguationData":[TD([[makeQuery(id+"F47.imprint","IMPRINT",EDGE,{"derivedFrom":sQuery(id+"F47.wireOp",EDGE,"E104.MirrorCS")}),-1.0]])]});
            var Q1;
            Q1=makeQuery(id+"F48.imprint","IMPRINT",FACE,{"disambiguationData":[TD([[makeQuery(id+"F48.imprint","IMPRINT",EDGE,{"derivedFrom":sQuery(id+"F48.wireOp",EDGE,"E118.MirrorCS")}),-1.0]])]});
            loft(context, id + "F49", {"sheetProfilesArray" : [{ "sheetProfileEntities" : qUnion([Q0]) }, { "sheetProfileEntities" : qUnion([Q1]) }]});
        }
        {
            var Q0;
            Q0=makeQuery(id+"F49.opLoft","SWEPT_BODY",BODY,{"disambiguationData":[OSD([makeQuery(id+"F47.imprint","IMPRINT",FACE,{"disambiguationData":[TD([[makeQuery(id+"F47.imprint","IMPRINT",EDGE,{"derivedFrom":sQuery(id+"F47.wireOp",EDGE,"E104.MirrorCS")}),-1.0]])]}),makeQuery(id+"F48.imprint","IMPRINT",FACE,{"disambiguationData":[TD([[makeQuery(id+"F48.imprint","IMPRINT",EDGE,{"derivedFrom":sQuery(id+"F48.wireOp",EDGE,"E118.MirrorCS")}),-1.0]])]})])]});
            var Q1;
            Q1=qCreatedBy(makeId("Right.planeOp"),FACE);
            mirror(context, id + "F50", {"entities" : qUnion([Q0]), "mirrorPlane" : qUnion([Q1])});
        }
        {
            var Q0;
            Q0=qCreatedBy(makeId("Right.planeOp"),FACE);
            var sketch = newSketch(context, id + "F51", { "sketchPlane" : qUnion([Q0])});
            skPoint(sketch, "E122.0", {"position": v(953.06, 1679.96) * mm});
            skLineSegment(sketch, "E123.bottom", {"start": v(953.06, 1679.96) * mm, "end": v(934, 1679.96) * mm});
            skLineSegment(sketch, "E123.top", {"start": v(953.06, 1641.86) * mm, "end": v(934, 1641.86) * mm});
            skLineSegment(sketch, "E123.left", {"start": v(953.06, 1679.96) * mm, "end": v(953.06, 1641.86) * mm});
            skArc(sketch, "E124", {"start": v(934, 1679.96) * mm, "mid": v(914.96, 1660.9) * mm, "end": v(934, 1641.86) * mm});
            skPoint(sketch, "E124.centerSnap0", {"position": v(934, 1679.96) * mm});
            skPoint(sketch, "E124.centerSnap1", {"position": v(914.96, 1660.9) * mm});
            skPoint(sketch, "E125.orphan", {"position": v(914.96, 1641.86) * mm});
            skPoint(sketch, "E123.right.start.orphan", {"position": v(914.96, 1679.96) * mm});
            skCircle(sketch, "E126", {"center": v(934, 1660.9) * mm, "radius": 3.18 * mm});
            skPoint(sketch, "E127.0", {"position": v(38.1, 1119.99) * mm});
            skLineSegment(sketch, "E128.bottom", {"start": v(38.1, 1119.99) * mm, "end": v(57.15, 1119.99) * mm});
            skLineSegment(sketch, "E128.top", {"start": v(38.1, 1081.89) * mm, "end": v(57.15, 1081.89) * mm});
            skLineSegment(sketch, "E128.left", {"start": v(38.1, 1119.99) * mm, "end": v(38.1, 1081.89) * mm});
            skArc(sketch, "E129", {"start": v(57.15, 1081.89) * mm, "mid": v(76.2, 1100.94) * mm, "end": v(57.15, 1119.99) * mm});
            skPoint(sketch, "E129.centerSnap0", {"position": v(76.2, 1100.94) * mm});
            skPoint(sketch, "E129.centerSnap1", {"position": v(57.15, 1119.99) * mm});
            skPoint(sketch, "E130.orphan", {"position": v(76.2, 1119.99) * mm});
            skPoint(sketch, "E131.orphan", {"position": v(76.2, 1081.89) * mm});
            skCircle(sketch, "E132", {"center": v(57.15, 1100.94) * mm, "radius": 3.18 * mm});
            skSolve(sketch);
        }
        {
            var Q0;
            Q0 = qSketchRegion(id + "F51", true);
            extrude(context, id + "F52", {"entities" : qUnion([Q0]), "depth" : 38.1 * mm, "symmetric" : true});
        }
        {
            var Q0;
            Q0=makeQuery(id+"F52.opExtrude","CAP_FACE",FACE,{"disambiguationData":[OSD([sQuery(id+"F51.wireOp",EDGE,"E128.bottom"),sQuery(id+"F51.wireOp",EDGE,"E128.top"),sQuery(id+"F51.wireOp",EDGE,"E128.left"),sQuery(id+"F51.wireOp",EDGE,"E129"),sQuery(id+"F51.wireOp",EDGE,"E132")])],"isStart":false});
            var sketch = newSketch(context, id + "F53", { "sketchPlane" : qUnion([Q0])});
            skCircle(sketch, "E133.0", {"center": v(934, 1660.9) * mm, "radius": 3.18 * mm, "construction": true});
            skCircle(sketch, "E134.0", {"center": v(57.15, 1100.94) * mm, "radius": 3.18 * mm, "construction": true});
            skLineSegment(sketch, "E135", {"start": v(57.15, 1100.94) * mm, "end": v(934, 1660.9) * mm, "construction": true});
            skLineSegment(sketch, "E136.bottom", {"start": v(147.68, 1136.15) * mm, "end": v(67.4, 1084.88) * mm});
            skLineSegment(sketch, "E136.top", {"start": v(127.17, 1168.26) * mm, "end": v(46.9, 1117) * mm});
            skLineSegment(sketch, "E136.left", {"start": v(147.68, 1136.15) * mm, "end": v(127.17, 1168.26) * mm});
            skArc(sketch, "E137", {"start": v(46.9, 1117) * mm, "mid": v(41.1, 1090.68) * mm, "end": v(67.4, 1084.88) * mm});
            skPoint(sketch, "E138.orphan", {"position": v(-33.38, 1065.73) * mm});
            skPoint(sketch, "E139.orphan", {"position": v(-12.87, 1033.62) * mm});
            skCircle(sketch, "E140", {"center": v(121.37, 1141.95) * mm, "radius": 4.2 * mm});
            skCircle(sketch, "E141", {"center": v(89.26, 1121.44) * mm, "radius": 4.2 * mm});
            skCircle(sketch, "E142", {"center": v(57.15, 1100.94) * mm, "radius": 4.2 * mm});
            skLineSegment(sketch, "E143.bottom", {"start": v(843.48, 1625.7) * mm, "end": v(923.76, 1676.96) * mm});
            skLineSegment(sketch, "E143.top", {"start": v(863.98, 1593.59) * mm, "end": v(944.26, 1644.85) * mm});
            skLineSegment(sketch, "E143.left", {"start": v(843.48, 1625.7) * mm, "end": v(863.98, 1593.59) * mm});
            skArc(sketch, "E144", {"start": v(944.26, 1644.85) * mm, "mid": v(950.06, 1671.16) * mm, "end": v(923.76, 1676.96) * mm});
            skPoint(sketch, "E145.orphan", {"position": v(1004.03, 1728.23) * mm});
            skPoint(sketch, "E146.orphan", {"position": v(1024.54, 1696.12) * mm});
            skCircle(sketch, "E147", {"center": v(869.79, 1619.9) * mm, "radius": 4.2 * mm});
            skCircle(sketch, "E148", {"center": v(901.9, 1640.4) * mm, "radius": 4.2 * mm});
            skCircle(sketch, "E149", {"center": v(934, 1660.9) * mm, "radius": 4.2 * mm});
            skSolve(sketch);
        }
        {
            var Q0;
            Q0 = qSketchRegion(id + "F53", true);
            extrude(context, id + "F54", {"entities" : qUnion([Q0]), "depth" : 6.35 * mm});
        }
        {
            var Q0;
            Q0=makeQuery(id+"F54.opExtrude","SWEPT_BODY",BODY,{"disambiguationData":[OSD([sQuery(id+"F53.wireOp",EDGE,"E143.bottom"),sQuery(id+"F53.wireOp",EDGE,"E143.top"),sQuery(id+"F53.wireOp",EDGE,"E143.left"),sQuery(id+"F53.wireOp",EDGE,"E144"),sQuery(id+"F53.wireOp",EDGE,"E147"),sQuery(id+"F53.wireOp",EDGE,"E148"),sQuery(id+"F53.wireOp",EDGE,"E149")])]});
            var Q1;
            Q1=makeQuery(id+"F54.opExtrude","SWEPT_BODY",BODY,{"disambiguationData":[OSD([sQuery(id+"F53.wireOp",EDGE,"E136.bottom"),sQuery(id+"F53.wireOp",EDGE,"E136.top"),sQuery(id+"F53.wireOp",EDGE,"E136.left"),sQuery(id+"F53.wireOp",EDGE,"E137"),sQuery(id+"F53.wireOp",EDGE,"E140"),sQuery(id+"F53.wireOp",EDGE,"E141"),sQuery(id+"F53.wireOp",EDGE,"E142")])]});
            var Q2;
            Q2=qCreatedBy(makeId("Right.planeOp"),FACE);
            mirror(context, id + "F55", {"entities" : qUnion([Q0, Q1]), "mirrorPlane" : qUnion([Q2])});
        }
        {
            var Q0;
            Q0=makeQuery(id+"F55.opPattern","COPY",FACE,{"derivedFrom":makeQuery(id+"F54.opExtrude","CAP_FACE",FACE,{"disambiguationData":[OSD([sQuery(id+"F53.wireOp",EDGE,"E136.bottom"),sQuery(id+"F53.wireOp",EDGE,"E136.top"),sQuery(id+"F53.wireOp",EDGE,"E136.left"),sQuery(id+"F53.wireOp",EDGE,"E137"),sQuery(id+"F53.wireOp",EDGE,"E140"),sQuery(id+"F53.wireOp",EDGE,"E141"),sQuery(id+"F53.wireOp",EDGE,"E142")])],"isStart":true}),"instanceName":"1"});
            var sketch = newSketch(context, id + "F56", { "sketchPlane" : qUnion([Q0])});
            skLineSegment(sketch, "E150.bottom", {"start": v(68.3, 1130.66) * mm, "end": v(902.35, 1663.3) * mm});
            skLineSegment(sketch, "E150.top", {"start": v(88.81, 1098.55) * mm, "end": v(922.85, 1631.18) * mm});
            skLineSegment(sketch, "E150.left", {"start": v(68.3, 1130.66) * mm, "end": v(88.81, 1098.55) * mm});
            skLineSegment(sketch, "E150.right", {"start": v(902.35, 1663.3) * mm, "end": v(922.85, 1631.18) * mm});
            skSolve(sketch);
        }
        {
            var Q0;
            Q0 = qSketchRegion(id + "F56", true);
            extrude(context, id + "F57", {"entities" : qUnion([Q0]), "depth" : 38.1 * mm});
        }
        {
            var Q0;
            Q0=makeQuery(id+"F6.imprint","IMPRINT",FACE,{"disambiguationData":[TD([[makeQuery(id+"F6.imprint","IMPRINT",EDGE,{"derivedFrom":sQuery(id+"F6.wireOp",EDGE,"E43")}),1.0]])]});
            extrude(context, id + "F58", {"entities" : qUnion([Q0]), "oppositeDirection" : true, "depth" : 38.1 * mm});
        }
        {
            var Q0;
            Q0=qCreatedBy(id+"F14.planeOp",FACE);
            var sketch = newSketch(context, id + "F59", { "sketchPlane" : qUnion([Q0])});
            skLineSegment(sketch, "E151.0.0", {"start": v(0, 290.98) * mm, "end": v(-694.28, 290.98) * mm});
            skLineSegment(sketch, "E151.0.1", {"start": v(-694.28, 290.98) * mm, "end": v(-689.79, 214.78) * mm});
            skLineSegment(sketch, "E151.0.2", {"start": v(-689.79, 214.78) * mm, "end": v(0, 214.78) * mm});
            skLineSegment(sketch, "E151.0.3", {"start": v(0, 214.78) * mm, "end": v(689.79, 214.78) * mm});
            skLineSegment(sketch, "E151.0.4", {"start": v(689.79, 214.78) * mm, "end": v(694.28, 290.98) * mm});
            skLineSegment(sketch, "E151.0.5", {"start": v(694.28, 290.98) * mm, "end": v(0, 290.98) * mm});
            skSolve(sketch);
        }
        {
            var Q0;
            Q0 = qSketchRegion(id + "F59", true);
            extrude(context, id + "F60", {"entities" : qUnion([Q0]), "oppositeDirection" : true, "depth" : 38.1 * mm});
        }
        {
            var Q0;
            Q0=qCreatedBy(id+"F23.planeOp",FACE);
            var sketch = newSketch(context, id + "F61", { "sketchPlane" : qUnion([Q0])});
            skLineSegment(sketch, "E152.0.0", {"start": v(689.79, 214.78) * mm, "end": v(694.28, 290.98) * mm});
            skLineSegment(sketch, "E152.0.1", {"start": v(694.28, 290.98) * mm, "end": v(-694.28, 290.98) * mm});
            skLineSegment(sketch, "E152.0.2", {"start": v(-694.28, 290.98) * mm, "end": v(-689.79, 214.78) * mm});
            skLineSegment(sketch, "E152.0.3", {"start": v(-689.79, 214.78) * mm, "end": v(689.79, 214.78) * mm});
            skSolve(sketch);
        }
        {
            var Q0;
            Q0 = qSketchRegion(id + "F61", true);
            extrude(context, id + "F62", {"entities" : qUnion([Q0]), "oppositeDirection" : true, "depth" : 38.1 * mm});
        }
        {
            var Q0;
            Q0=qCreatedBy(makeId("Front.planeOp"),FACE);
            var sketch = newSketch(context, id + "F63", { "sketchPlane" : qUnion([Q0])});
            skLineSegment(sketch, "E153.0.0", {"start": v(694.28, 290.98) * mm, "end": v(689.79, 214.78) * mm});
            skLineSegment(sketch, "E153.0.1", {"start": v(689.79, 214.78) * mm, "end": v(-689.79, 214.78) * mm});
            skLineSegment(sketch, "E153.0.2", {"start": v(-689.79, 214.78) * mm, "end": v(-694.28, 290.98) * mm});
            skLineSegment(sketch, "E153.0.3", {"start": v(-694.28, 290.98) * mm, "end": v(694.28, 290.98) * mm});
            skSolve(sketch);
        }
        {
            var Q0;
            Q0 = qSketchRegion(id + "F63", true);
            extrude(context, id + "F64", {"entities" : qUnion([Q0]), "oppositeDirection" : true, "depth" : 38.1 * mm});
        }
        {
            var Q0;
            {var subQ2=sQuery(id+"F6.wireOp",EDGE,"E18");Q0=makeQuery(id+"F6.imprint","IMPRINT",FACE,{"disambiguationData":[TD([[makeQuery(id+"F6.imprint","IMPRINT",EDGE,{"derivedFrom":subQ2}),-1.0]])]});}
            var sketch = newSketch(context, id + "F65", { "sketchPlane" : qUnion([Q0])});
            skLineSegment(sketch, "E154.0", {"start": v(689.79, 214.78) * mm, "end": v(0, 214.78) * mm, "construction": true});
            skLineSegment(sketch, "E155.0", {"start": v(-717.55, 38.1) * mm, "end": v(717.55, 38.1) * mm, "construction": true});
            skLineSegment(sketch, "E156.bottom", {"start": v(19.05, 214.78) * mm, "end": v(-19.05, 214.78) * mm});
            skLineSegment(sketch, "E156.top", {"start": v(19.05, 38.1) * mm, "end": v(-19.05, 38.1) * mm});
            skLineSegment(sketch, "E156.left", {"start": v(19.05, 214.78) * mm, "end": v(19.05, 38.1) * mm});
            skLineSegment(sketch, "E156.right", {"start": v(-19.05, 214.78) * mm, "end": v(-19.05, 38.1) * mm});
            skPoint(sketch, "E156.middle", {"position": v(0, 126.44) * mm});
            skSolve(sketch);
        }
        {
            var Q0;
            Q0 = qSketchRegion(id + "F65", true);
            extrude(context, id + "F66", {"entities" : qUnion([Q0]), "oppositeDirection" : true, "depth" : 38.1 * mm});
        }
        {
            var Q0;
            Q0=qCreatedBy(makeId("Front.planeOp"),FACE);
            var sketch = newSketch(context, id + "F67", { "sketchPlane" : qUnion([Q0])});
            skLineSegment(sketch, "E157.0.0", {"start": v(-19.05, 214.78) * mm, "end": v(19.05, 214.78) * mm});
            skLineSegment(sketch, "E157.0.1", {"start": v(19.05, 214.78) * mm, "end": v(19.05, 38.1) * mm});
            skLineSegment(sketch, "E157.0.2", {"start": v(19.05, 38.1) * mm, "end": v(-19.05, 38.1) * mm});
            skLineSegment(sketch, "E157.0.3", {"start": v(-19.05, 38.1) * mm, "end": v(-19.05, 214.78) * mm});
            skSolve(sketch);
        }
        {
            var Q0;
            Q0 = qSketchRegion(id + "F67", true);
            extrude(context, id + "F68", {"entities" : qUnion([Q0]), "oppositeDirection" : true, "depth" : 38.1 * mm});
        }
        {
            var Q0;
            Q0=makeQuery(id+"F64.opExtrude","CAP_FACE",FACE,{"disambiguationData":[OSD([sQuery(id+"F63.wireOp",EDGE,"E153.0.0"),sQuery(id+"F63.wireOp",EDGE,"E153.0.1"),sQuery(id+"F63.wireOp",EDGE,"E153.0.2"),sQuery(id+"F63.wireOp",EDGE,"E153.0.3")])],"isStart":false});
            var sketch = newSketch(context, id + "F69", { "sketchPlane" : qUnion([Q0])});
            skLineSegment(sketch, "E158.bottom", {"start": v(19.05, 290.98) * mm, "end": v(-19.05, 290.98) * mm});
            skLineSegment(sketch, "E158.top", {"start": v(19.05, 252.88) * mm, "end": v(-19.05, 252.88) * mm});
            skLineSegment(sketch, "E158.left", {"start": v(19.05, 290.98) * mm, "end": v(19.05, 252.88) * mm});
            skLineSegment(sketch, "E158.right", {"start": v(-19.05, 290.98) * mm, "end": v(-19.05, 252.88) * mm});
            skPoint(sketch, "E158.middle", {"position": v(0, 271.93) * mm});
            skPoint(sketch, "E158.middle.positionSnap0", {"position": v(0, 290.98) * mm});
            skPoint(sketch, "E158.centerSnap0", {"position": v(0, 290.98) * mm});
            skSolve(sketch);
        }
        {
            var Q0;
            Q0 = qSketchRegion(id + "F69", true);
            var Q1;
            Q1=makeQuery(id+"F62.opExtrude","CAP_FACE",FACE,{"disambiguationData":[OSD([sQuery(id+"F61.wireOp",EDGE,"E152.0.0"),sQuery(id+"F61.wireOp",EDGE,"E152.0.1"),sQuery(id+"F61.wireOp",EDGE,"E152.0.2"),sQuery(id+"F61.wireOp",EDGE,"E152.0.3")])],"isStart":false});
            extrude(context, id + "F70", {"entities" : qUnion([Q0]), "endBound" : BoundingType.UP_TO_SURFACE, "endBoundEntityFace" : qUnion([Q1]), "depth" : 25.4 * mm});
        }
        {
            var Q0;
            Q0=makeQuery(id+"F62.opExtrude","CAP_FACE",FACE,{"disambiguationData":[OSD([sQuery(id+"F61.wireOp",EDGE,"E152.0.0"),sQuery(id+"F61.wireOp",EDGE,"E152.0.1"),sQuery(id+"F61.wireOp",EDGE,"E152.0.2"),sQuery(id+"F61.wireOp",EDGE,"E152.0.3")])],"isStart":true});
            var sketch = newSketch(context, id + "F71", { "sketchPlane" : qUnion([Q0])});
            skPoint(sketch, "E159", {"position": v(-231.49, 271.93) * mm});
            skPoint(sketch, "E160", {"position": v(231.49, 271.93) * mm});
            skPoint(sketch, "E161.0", {"position": v(-694.28, 290.98) * mm});
            skPoint(sketch, "E162.0", {"position": v(694.28, 290.98) * mm});
            skLineSegment(sketch, "E163.bottom", {"start": v(-212.44, 290.98) * mm, "end": v(-250.54, 290.98) * mm});
            skLineSegment(sketch, "E163.top", {"start": v(-212.44, 252.88) * mm, "end": v(-250.54, 252.88) * mm});
            skLineSegment(sketch, "E163.left", {"start": v(-212.44, 290.98) * mm, "end": v(-212.44, 252.88) * mm});
            skLineSegment(sketch, "E163.right", {"start": v(-250.54, 290.98) * mm, "end": v(-250.54, 252.88) * mm});
            skLineSegment(sketch, "E164.bottom", {"start": v(250.54, 290.98) * mm, "end": v(212.44, 290.98) * mm});
            skLineSegment(sketch, "E164.top", {"start": v(250.54, 252.88) * mm, "end": v(212.44, 252.88) * mm});
            skLineSegment(sketch, "E164.left", {"start": v(250.54, 290.98) * mm, "end": v(250.54, 252.88) * mm});
            skLineSegment(sketch, "E164.right", {"start": v(212.44, 290.98) * mm, "end": v(212.44, 252.88) * mm});
            skSolve(sketch);
        }
        {
            var Q0;
            Q0 = qSketchRegion(id + "F71", true);
            var Q1;
            Q1=makeQuery(id+"F60.opExtrude","CAP_FACE",FACE,{"disambiguationData":[OSD([sQuery(id+"F59.wireOp",EDGE,"E151.0.0"),sQuery(id+"F59.wireOp",EDGE,"E151.0.1"),sQuery(id+"F59.wireOp",EDGE,"E151.0.2"),sQuery(id+"F59.wireOp",EDGE,"E151.0.3"),sQuery(id+"F59.wireOp",EDGE,"E151.0.4"),sQuery(id+"F59.wireOp",EDGE,"E151.0.5")])],"isStart":false});
            extrude(context, id + "F72", {"entities" : qUnion([Q0]), "endBound" : BoundingType.UP_TO_SURFACE, "endBoundEntityFace" : qUnion([Q1]), "depth" : 25.4 * mm});
        }
        {
            var Q0;
            Q0=makeQuery(id+"F60.opExtrude","CAP_FACE",FACE,{"disambiguationData":[OSD([sQuery(id+"F59.wireOp",EDGE,"E151.0.0"),sQuery(id+"F59.wireOp",EDGE,"E151.0.1"),sQuery(id+"F59.wireOp",EDGE,"E151.0.2"),sQuery(id+"F59.wireOp",EDGE,"E151.0.3"),sQuery(id+"F59.wireOp",EDGE,"E151.0.4"),sQuery(id+"F59.wireOp",EDGE,"E151.0.5")])],"isStart":true});
            var sketch = newSketch(context, id + "F73", { "sketchPlane" : qUnion([Q0])});
            skLineSegment(sketch, "E165.0.0", {"start": v(-212.44, 290.98) * mm, "end": v(-250.54, 290.98) * mm});
            skLineSegment(sketch, "E165.0.1", {"start": v(-250.54, 290.98) * mm, "end": v(-250.54, 252.88) * mm});
            skLineSegment(sketch, "E165.0.2", {"start": v(-250.54, 252.88) * mm, "end": v(-212.44, 252.88) * mm});
            skLineSegment(sketch, "E165.0.3", {"start": v(-212.44, 252.88) * mm, "end": v(-212.44, 290.98) * mm});
            skLineSegment(sketch, "E166.0.0", {"start": v(250.54, 290.98) * mm, "end": v(212.44, 290.98) * mm});
            skLineSegment(sketch, "E166.0.1", {"start": v(212.44, 290.98) * mm, "end": v(212.44, 252.88) * mm});
            skLineSegment(sketch, "E166.0.2", {"start": v(212.44, 252.88) * mm, "end": v(250.54, 252.88) * mm});
            skLineSegment(sketch, "E166.0.3", {"start": v(250.54, 252.88) * mm, "end": v(250.54, 290.98) * mm});
            skSolve(sketch);
        }
        {
            var Q0;
            Q0 = qSketchRegion(id + "F73", true);
            var Q1;
            Q1=makeQuery(id+"F58.opExtrude","CAP_FACE",FACE,{"disambiguationData":[OSD([sQuery(id+"F6.wireOp",EDGE,"E43"),sQuery(id+"F6.wireOp",EDGE,"E44"),sQuery(id+"F6.wireOp",EDGE,"E45"),sQuery(id+"F6.wireOp",EDGE,"E46.MirrorCS"),sQuery(id+"F6.wireOp",EDGE,"E47.MirrorCS"),sQuery(id+"F6.wireOp",EDGE,"E48.MirrorCS")])],"isStart":false});
            extrude(context, id + "F74", {"entities" : qUnion([Q0]), "endBound" : BoundingType.UP_TO_SURFACE, "endBoundEntityFace" : qUnion([Q1]), "depth" : 25.4 * mm});
        }
        {
            var Q0;
            Q0=makeQuery(id+"F58.opExtrude","SWEPT_FACE",FACE,{"disambiguationData":[OSD([sQuery(id+"F6.wireOp",EDGE,"E43"),sQuery(id+"F6.wireOp",EDGE,"E47.MirrorCS")])]});
            var sketch = newSketch(context, id + "F75", { "sketchPlane" : qUnion([Q0])});
            skLineSegment(sketch, "E167.bottom", {"start": v(694.28, 1657.35) * mm, "end": v(-694.28, 1657.35) * mm});
            skLineSegment(sketch, "E167.top", {"start": v(694.28, 0) * mm, "end": v(-694.28, 0) * mm});
            skLineSegment(sketch, "E167.left", {"start": v(694.28, 1657.35) * mm, "end": v(694.28, 0) * mm});
            skLineSegment(sketch, "E167.right", {"start": v(-694.28, 1657.35) * mm, "end": v(-694.28, 0) * mm});
            skPoint(sketch, "E168.0", {"position": v(-694.28, 0) * mm});
            skSolve(sketch);
        }
        {
            var Q0;
            Q0 = qSketchRegion(id + "F75", true);
            extrude(context, id + "F76", {"entities" : qUnion([Q0]), "depth" : 12.7 * mm});
        }
        {
            var Q0;
            Q0=makeQuery(id+"F27.opPattern","COPY",FACE,{"derivedFrom":makeQuery(id+"F26.opExtrude","SWEPT_FACE",FACE,{"disambiguationData":[OSD([sQuery(id+"F24.wireOp",EDGE,"E70")])]}),"instanceName":"1"});
            var sketch = newSketch(context, id + "F77", { "sketchPlane" : qUnion([Q0])});
            skCircle(sketch, "E169", {"center": v(-866.62, 392) * mm, "radius": 3.18 * mm});
            skPoint(sketch, "E169.centerSnap0", {"position": v(-866.62, 411.05) * mm});
            skPoint(sketch, "E169.centerSnap1", {"position": v(-885.67, 392) * mm});
            skSolve(sketch);
        }
        {
            var Q0;
            Q0 = qSketchRegion(id + "F77", true);
            extrude(context, id + "F78", {"entities" : qUnion([Q0]), "operationType" : NewBodyOperationType.REMOVE, "oppositeDirection" : true, "depth" : 25.4 * mm});
        }
        {
            var Q0;
            Q0=makeQuery(id+"F26.opExtrude","SWEPT_FACE",FACE,{"disambiguationData":[OSD([sQuery(id+"F24.wireOp",EDGE,"E70")])]});
            var sketch = newSketch(context, id + "F79", { "sketchPlane" : qUnion([Q0])});
            skCircle(sketch, "E170", {"center": v(866.62, 392) * mm, "radius": 3.18 * mm});
            skPoint(sketch, "E170.centerSnap0", {"position": v(866.62, 411.05) * mm});
            skPoint(sketch, "E170.centerSnap1", {"position": v(847.57, 392) * mm});
            skSolve(sketch);
        }
        {
            var Q0;
            Q0 = qSketchRegion(id + "F79", true);
            extrude(context, id + "F80", {"entities" : qUnion([Q0]), "operationType" : NewBodyOperationType.REMOVE, "oppositeDirection" : true, "depth" : 25.4 * mm});
        }
        {
            var Q0;
            Q0=makeQuery(id+"F42.opExtrude","SWEPT_FACE",FACE,{"disambiguationData":[OSD([sQuery(id+"F16.wireOp",EDGE,"E64")])]});
            var sketch = newSketch(context, id + "F81", { "sketchPlane" : qUnion([Q0])});
            skCircle(sketch, "E171", {"center": v(972.1, 1457.52) * mm, "radius": 3.18 * mm});
            skPoint(sketch, "E171.centerSnap0", {"position": v(991.16, 1457.52) * mm});
            skPoint(sketch, "E171.centerSnap1", {"position": v(972.1, 1476.57) * mm});
            skSolve(sketch);
        }
        {
            var Q0;
            Q0 = qSketchRegion(id + "F81", true);
            extrude(context, id + "F82", {"entities" : qUnion([Q0]), "operationType" : NewBodyOperationType.REMOVE, "oppositeDirection" : true, "depth" : 25.4 * mm});
        }
        {
            var Q0;
            Q0=makeQuery(id+"F43.opPattern","COPY",FACE,{"derivedFrom":makeQuery(id+"F42.opExtrude","SWEPT_FACE",FACE,{"disambiguationData":[OSD([sQuery(id+"F16.wireOp",EDGE,"E64")])]}),"instanceName":"1"});
            var sketch = newSketch(context, id + "F83", { "sketchPlane" : qUnion([Q0])});
            skCircle(sketch, "E172", {"center": v(-972.1, 1457.52) * mm, "radius": 3.18 * mm});
            skPoint(sketch, "E172.centerSnap0", {"position": v(-953.06, 1457.52) * mm});
            skPoint(sketch, "E172.centerSnap1", {"position": v(-972.1, 1476.57) * mm});
            skSolve(sketch);
        }
        {
            var Q0;
            Q0 = qSketchRegion(id + "F83", true);
            extrude(context, id + "F84", {"entities" : qUnion([Q0]), "operationType" : NewBodyOperationType.REMOVE, "oppositeDirection" : true, "depth" : 25.4 * mm});
        }
    });
